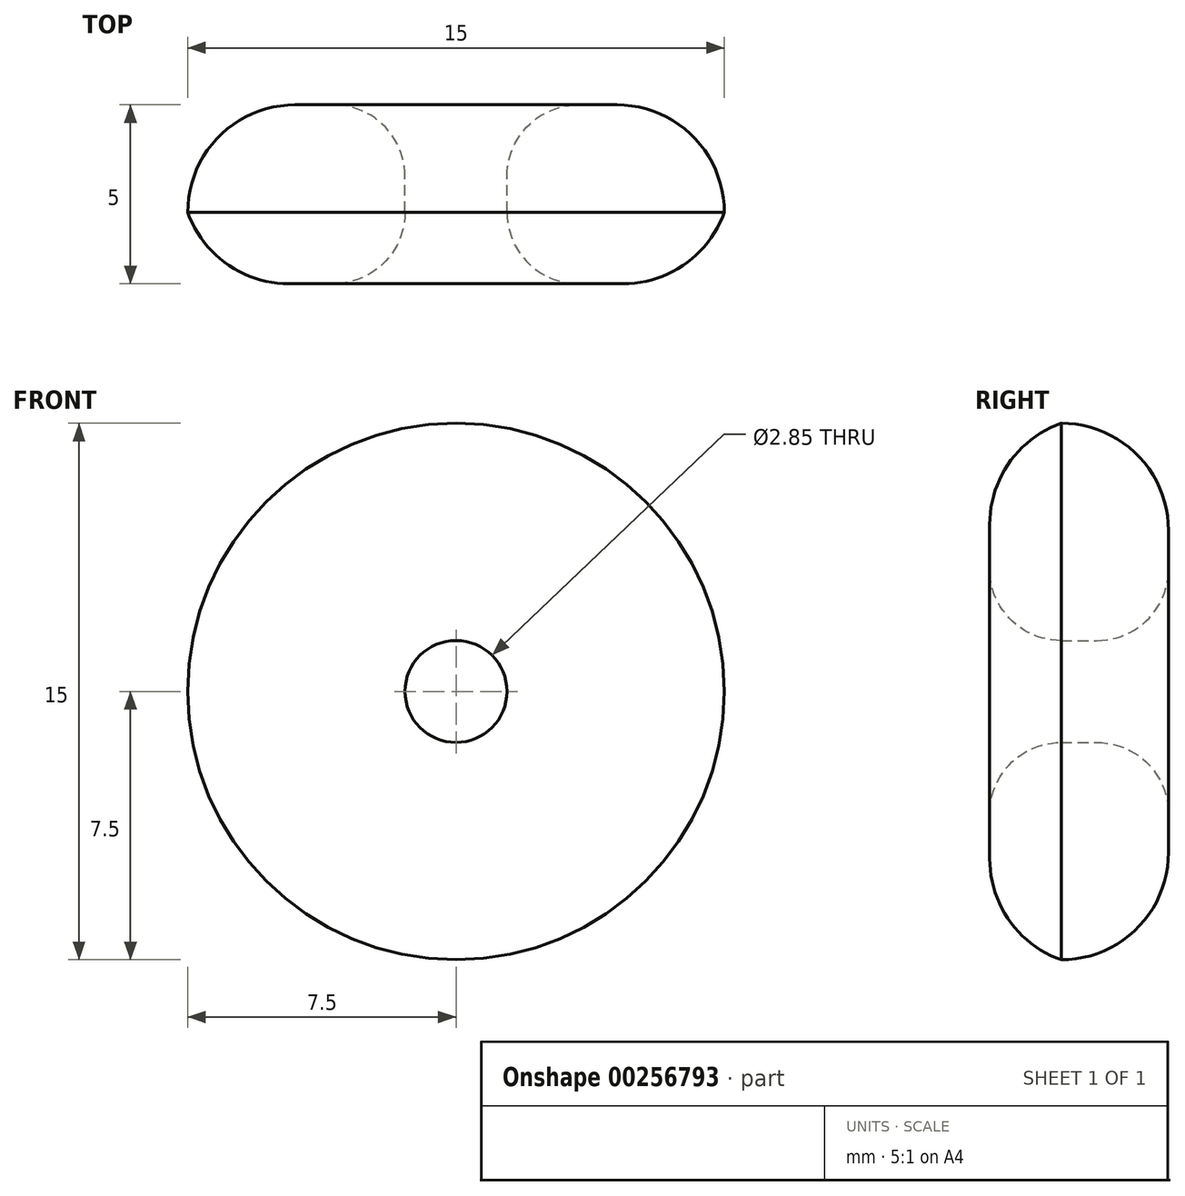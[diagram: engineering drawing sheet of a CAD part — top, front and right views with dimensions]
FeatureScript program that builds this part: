
annotation { "Feature Type Name" : "Feature", "Feature Type Description" : "" }
export const myFeature = defineFeature(function(context is Context, id is Id, definition is map)
    precondition{}
    {
        {
            var Q0;
            Q0=qCreatedBy(makeId("Front.planeOp"),FACE);
            var sketch = newSketch(context, id + "F0", { "sketchPlane" : qUnion([Q0])});
            skPoint(sketch, "E0.middle", {"position": v(0, 0) * mm});
            skPoint(sketch, "E0.right.start.orphan", {"position": v(50, 20) * mm});
            skPoint(sketch, "E1.end.orphan", {"position": v(42, -20) * mm});
            skPoint(sketch, "E1.start.orphan", {"position": v(50, -20) * mm});
            skPoint(sketch, "E0.left.start.orphan", {"position": v(-50, 20) * mm});
            skPoint(sketch, "E0.top.start.orphan", {"position": v(-50, -20) * mm});
            skCircle(sketch, "E2", {"center": v(0, 0) * mm, "radius": 7.5 * mm});
            skCircle(sketch, "E3", {"center": v(0, 0) * mm, "radius": 1.43 * mm});
            skSolve(sketch);
        }
        {
            var Q0;
            Q0=makeQuery(id+"F0.imprint","IMPRINT",FACE,{"disambiguationData":[TD([[makeQuery(id+"F0.imprint","IMPRINT",EDGE,{"derivedFrom":sQuery(id+"F0.wireOp",EDGE,"E2")}),1.0]])]});
            extrude(context, id + "F1", {"entities" : qUnion([Q0]), "depth" : 5 * mm});
        }
        {
            var Q0;
            Q0=makeQuery(id+"F1.opExtrude","CAP_EDGE",EDGE,{"disambiguationData":[OSD([sQuery(id+"F0.wireOp",EDGE,"E2")])],"isStart":true});
            fillet(context, id + "F2", {"entities" : qUnion([Q0]), "radius" : 3 * mm, "tangentPropagation" : true, "allowEdgeOverflow" : false});
        }
        {
            var Q0;
            Q0=makeQuery(id+"F1.opExtrude","CAP_EDGE",EDGE,{"disambiguationData":[OSD([sQuery(id+"F0.wireOp",EDGE,"E2")])],"isStart":false});
            fillet(context, id + "F3", {"entities" : qUnion([Q0]), "radius" : 3 * mm, "allowEdgeOverflow" : false});
        }
        {
            var Q0;
            Q0=makeQuery(id+"F1.opExtrude","SWEPT_FACE",FACE,{"disambiguationData":[OSD([sQuery(id+"F0.wireOp",EDGE,"E3")])]});
            fillet(context, id + "F4", {"entities" : qUnion([Q0]), "radius" : 2 * mm, "allowEdgeOverflow" : false});
        }
    });
